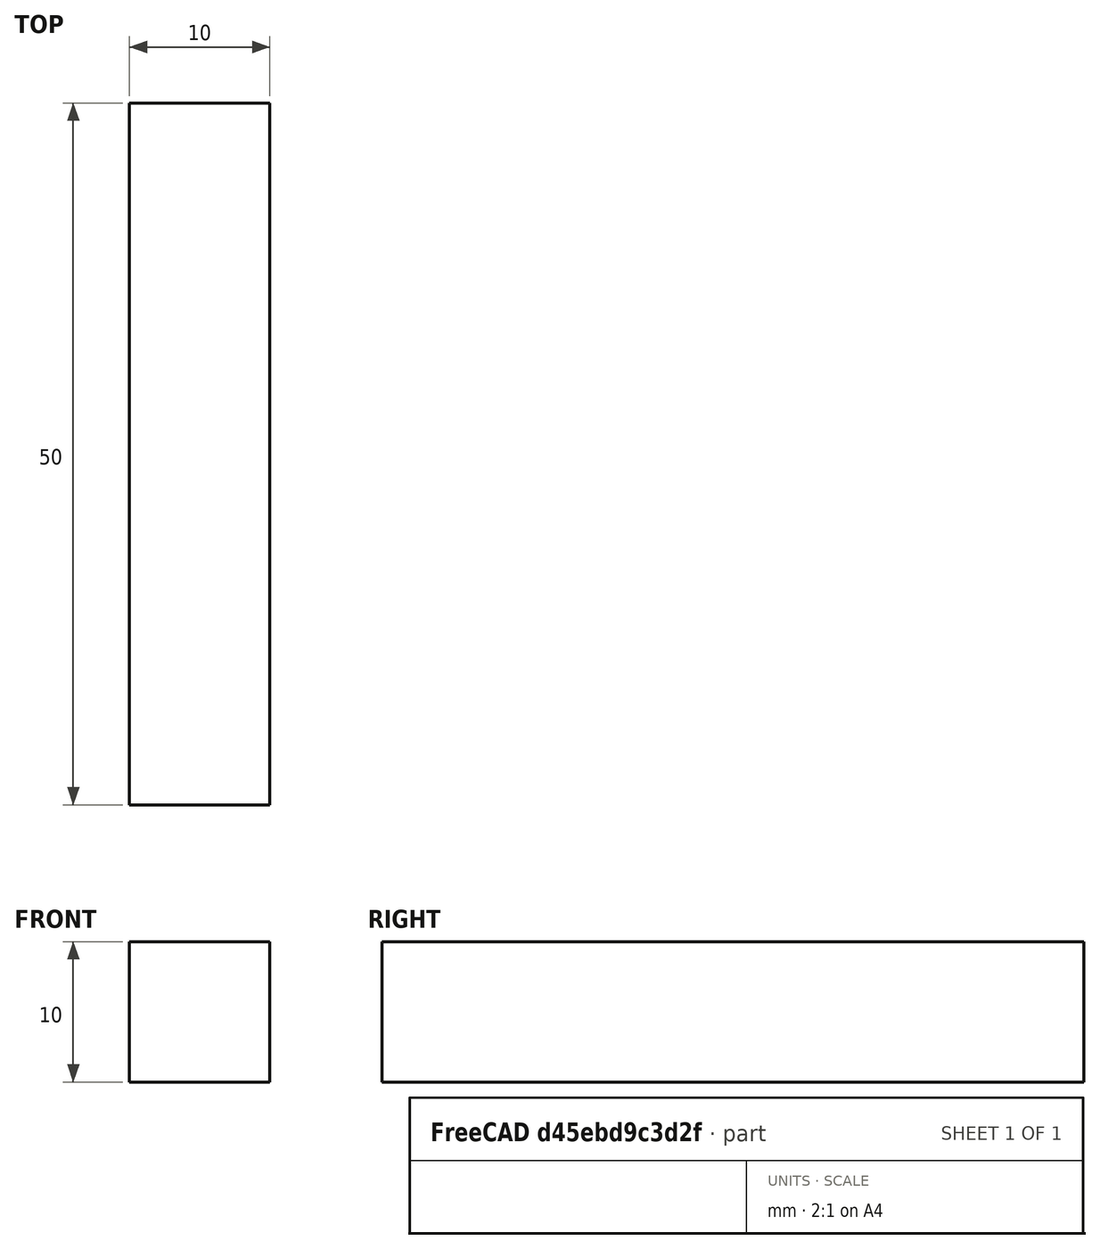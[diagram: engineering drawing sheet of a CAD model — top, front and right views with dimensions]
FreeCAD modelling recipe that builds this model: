
FCSTD DOCUMENT  (FreeCAD 0.16R)
Label: I
License: All rights reserved
LicenseURL: http://en.wikipedia.org/wiki/All_rights_reserved
objects: Sketcher::SketchObject×1, PartDesign::Pad×1, Mesh::Feature×1
note: 3 computed .brp shape members not serialized (recipe doc carries the construction recipe); baked Part::Feature solids carry a one-line shape summary decoded from their .brp

FEATURE [Sketcher::SketchObject] Sketch
  sketch-geometry (4):
    g0: LineSegment StartX=0 StartY=0 StartZ=0 EndX=0 EndY=50 EndZ=0
    g1: LineSegment StartX=0 StartY=50 StartZ=0 EndX=-10 EndY=50 EndZ=0
    g2: LineSegment StartX=-10 StartY=50 StartZ=0 EndX=-10 EndY=-1e-12 EndZ=0
    g3: LineSegment StartX=-10 StartY=-1e-12 StartZ=0 EndX=0 EndY=0 EndZ=0
  constraints (11):
    c: Coincident(g1,g2)
    c: Coincident(g2,g3)
    c: Coincident(g3,g0)
    c: Coincident(g1,g0)
    c: Distance(g1) = 10
    c: Distance(g0) = 50
    c: Equal(g0,g2)
    c: Distance(g3) = 10
    c: Vertical(g0)
    c: Horizontal(g1)
    c: Coincident(g0,g-1)
FEATURE [PartDesign::Pad] Pad
  Length = 10
  Length2 = 100
  Sketch = -> Sketch
  Type = 0
FEATURE [Mesh::Feature] Mesh  label="Pad (Meshed)"
